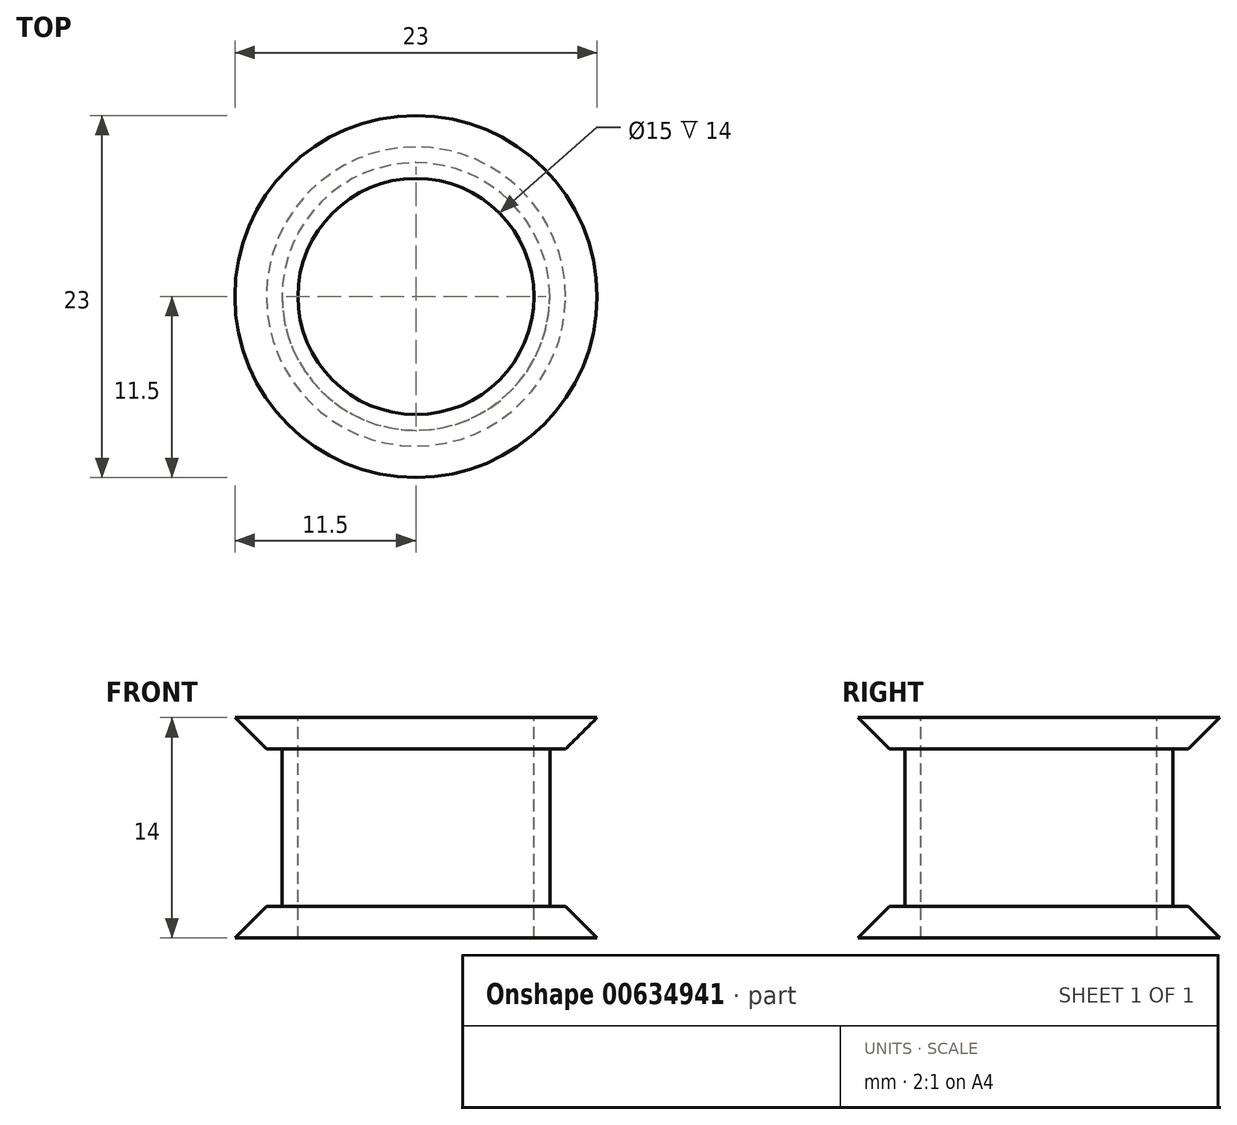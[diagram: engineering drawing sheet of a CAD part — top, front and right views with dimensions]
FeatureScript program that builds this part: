
annotation { "Feature Type Name" : "Feature", "Feature Type Description" : "" }
export const myFeature = defineFeature(function(context is Context, id is Id, definition is map)
    precondition{}
    {
        {
            var Q0;
            Q0=qCreatedBy(makeId("Top.planeOp"),FACE);
            var sketch = newSketch(context, id + "F0", { "sketchPlane" : qUnion([Q0])});
            skCircle(sketch, "E0", {"center": v(0, 0) * mm, "radius": 8.5 * mm});
            skSolve(sketch);
        }
        {
            var Q0;
            Q0=qSketchRegion(id+"F0",true);
            extrude(context, id + "F1", {"entities" : qUnion([Q0]), "depth" : 14 * mm, "offsetDistance" : 25 * mm});
        }
        {
            var Q0;
            Q0=makeQuery(id+"F1.opExtrude","CAP_FACE",FACE,{"disambiguationData":[OSD([sQuery(id+"F0.wireOp",EDGE,"E0")])],"isStart":false});
            var sketch = newSketch(context, id + "F2", { "sketchPlane" : qUnion([Q0])});
            skCircle(sketch, "E1", {"center": v(0, 0) * mm, "radius": 11.5 * mm});
            skSolve(sketch);
        }
        {
            var Q0;
            Q0=makeQuery(id+"F1.opExtrude","CAP_FACE",FACE,{"disambiguationData":[OSD([sQuery(id+"F0.wireOp",EDGE,"E0")])],"isStart":true});
            var sketch = newSketch(context, id + "F3", { "sketchPlane" : qUnion([Q0])});
            skCircle(sketch, "E2", {"center": v(0, 0) * mm, "radius": 11.5 * mm});
            skSolve(sketch);
        }
        {
            var Q0;
            Q0=makeQuery(id+"F2.imprint","IMPRINT",FACE,{"disambiguationData":[TD([[makeQuery(id+"F2.imprint","IMPRINT",EDGE,{"derivedFrom":sQuery(id+"F2.wireOp",EDGE,"E1")}),1.0]])]});
            extrude(context, id + "F4", {"entities" : qUnion([Q0]), "operationType" : NewBodyOperationType.ADD, "oppositeDirection" : true, "depth" : 2 * mm, "offsetDistance" : 25 * mm});
        }
        {
            var Q0;
            Q0=makeQuery(id+"F4.opExtrude","CAP_EDGE",EDGE,{"disambiguationData":[OSD([sQuery(id+"F2.wireOp",EDGE,"E1")])],"isStart":false});
            chamfer(context, id + "F5", {"entities" : qUnion([Q0]), "width" : 2 * mm, "tangentPropagation" : true});
        }
        {
            var Q0;
            Q0=makeQuery(id+"F3.imprint","IMPRINT",FACE,{"disambiguationData":[TD([[makeQuery(id+"F3.imprint","IMPRINT",EDGE,{"derivedFrom":sQuery(id+"F3.wireOp",EDGE,"E2")}),1.0]])]});
            extrude(context, id + "F6", {"entities" : qUnion([Q0]), "operationType" : NewBodyOperationType.ADD, "oppositeDirection" : true, "depth" : 2 * mm, "offsetDistance" : 25 * mm});
        }
        {
            var Q0;
            Q0=makeQuery(id+"F6.opExtrude","CAP_EDGE",EDGE,{"disambiguationData":[OSD([sQuery(id+"F3.wireOp",EDGE,"E2")])],"isStart":false});
            chamfer(context, id + "F7", {"entities" : qUnion([Q0]), "width" : 2 * mm, "tangentPropagation" : true});
        }
        {
            var Q0;
            {var subQ0=sQuery(id+"F0.wireOp",EDGE,"E0");Q0=makeQuery(id+"F4.boolean.opBoolean","MERGE",FACE,{"derivedFrom":[makeQuery(id+"F1.opExtrude","CAP_FACE",FACE,{"disambiguationData":[OSD([subQ0])],"isStart":false}),makeQuery(id+"F4.opExtrude","CAP_FACE",FACE,{"disambiguationData":[OSD([subQ0,sQuery(id+"F2.wireOp",EDGE,"E1")])],"isStart":true})]});}
            var sketch = newSketch(context, id + "F8", { "sketchPlane" : qUnion([Q0])});
            skCircle(sketch, "E3", {"center": v(0, 0) * mm, "radius": 7.5 * mm});
            skSolve(sketch);
        }
        {
            var Q0;
            Q0=qSketchRegion(id+"F8",true);
            extrude(context, id + "F9", {"entities" : qUnion([Q0]), "operationType" : NewBodyOperationType.REMOVE, "endBound" : BoundingType.THROUGH_ALL, "oppositeDirection" : true, "depth" : 25 * mm, "offsetDistance" : 25 * mm});
        }
    });
